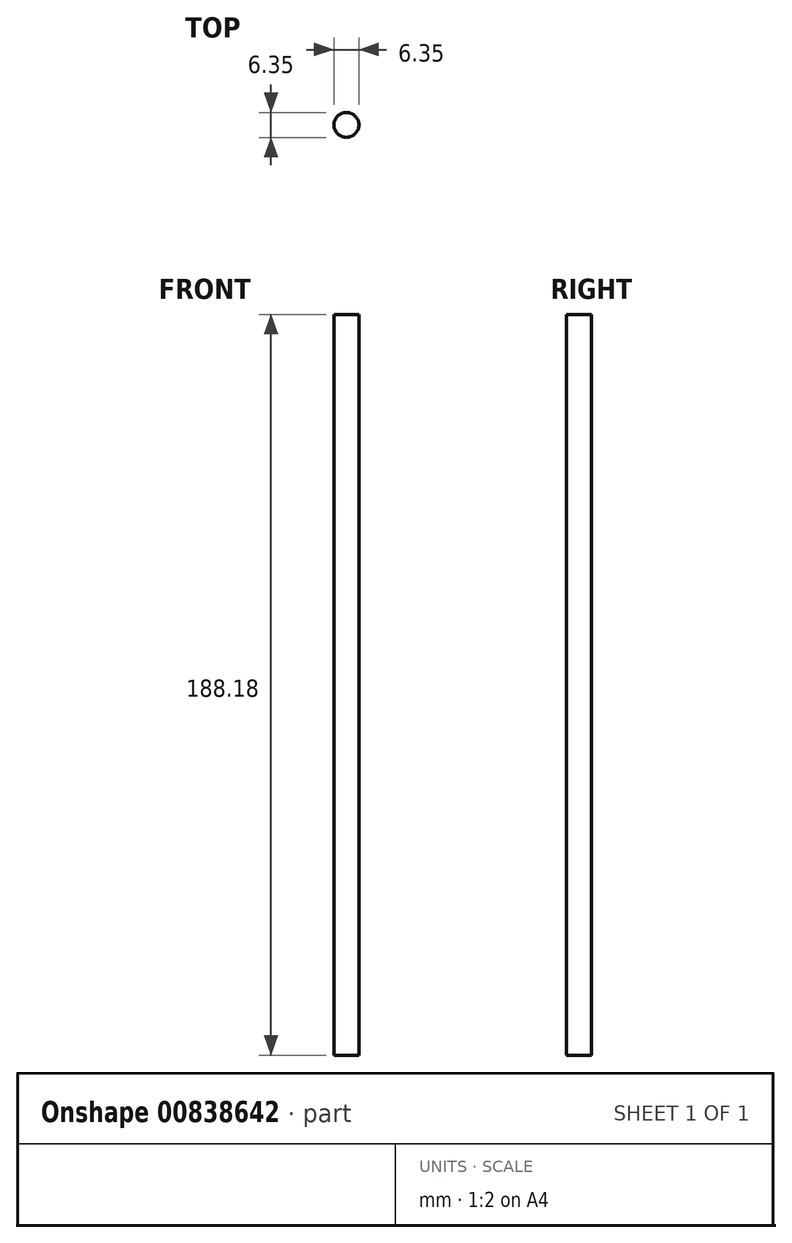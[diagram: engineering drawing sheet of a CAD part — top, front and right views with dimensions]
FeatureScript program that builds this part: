
annotation { "Feature Type Name" : "Feature", "Feature Type Description" : "" }
export const myFeature = defineFeature(function(context is Context, id is Id, definition is map)
    precondition{}
    {
        {
            var Q0;
            Q0=qCreatedBy(makeId("Top.planeOp"),FACE);
            var sketch = newSketch(context, id + "F0", { "sketchPlane" : qUnion([Q0])});
            skCircle(sketch, "E0", {"center": v(-74, 23.08) * mm, "radius": 3.18 * mm});
            skSolve(sketch);
        }
        {
            var Q0;
            Q0 = qSketchRegion(id + "F0", true);
            extrude(context, id + "F1", {"entities" : qUnion([Q0]), "depth" : 188.18 * mm, "offsetDistance" : 25.4 * mm});
        }
    });
